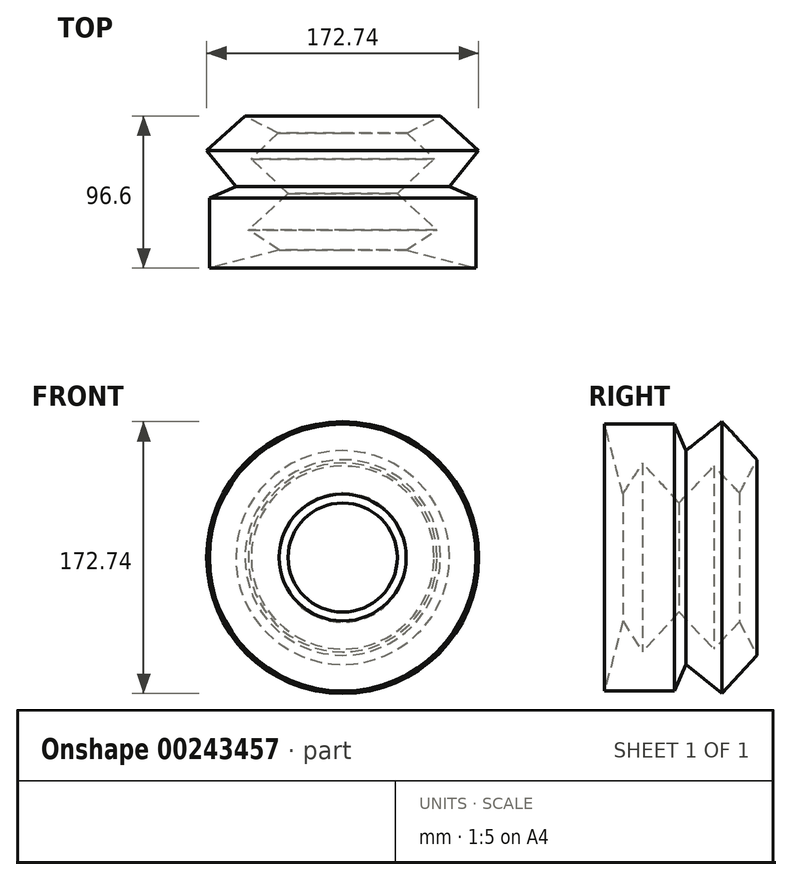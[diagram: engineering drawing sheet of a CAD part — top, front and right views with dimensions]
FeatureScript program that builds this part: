
annotation { "Feature Type Name" : "Feature", "Feature Type Description" : "" }
export const myFeature = defineFeature(function(context is Context, id is Id, definition is map)
    precondition{}
    {
        {
            var Q0;
            Q0=qCreatedBy(makeId("Top.planeOp"),FACE);
            var sketch = newSketch(context, id + "F0", { "sketchPlane" : qUnion([Q0])});
            skLineSegment(sketch, "E0", {"start": v(-10.73, 38.4) * mm, "end": v(6.44, 22.05) * mm});
            skLineSegment(sketch, "E1", {"start": v(6.44, 22.05) * mm, "end": v(-17, 0) * mm});
            skLineSegment(sketch, "E2", {"start": v(-17, 0) * mm, "end": v(8.26, -23.2) * mm});
            skLineSegment(sketch, "E3", {"start": v(8.26, -23.2) * mm, "end": v(-11.4, -35.75) * mm});
            skLineSegment(sketch, "E4", {"start": v(-11.4, -35.75) * mm, "end": v(33.03, -47.31) * mm});
            skLineSegment(sketch, "E5", {"start": v(33.03, -47.31) * mm, "end": v(33.03, -2.89) * mm});
            skLineSegment(sketch, "E6", {"start": v(33.03, -2.89) * mm, "end": v(16.18, 4.38) * mm});
            skLineSegment(sketch, "E7", {"start": v(16.18, 4.38) * mm, "end": v(34.68, 27.33) * mm});
            skLineSegment(sketch, "E8", {"start": v(34.68, 27.33) * mm, "end": v(10.4, 49.3) * mm});
            skLineSegment(sketch, "E9", {"start": v(10.4, 49.3) * mm, "end": v(-10.73, 38.4) * mm});
            skLineSegment(sketch, "E10", {"start": v(-51.69, 46) * mm, "end": v(-51.69, -40.05) * mm});
            skSolve(sketch);
        }
        {
            var Q0;
            Q0=makeQuery(id+"F0.imprint","IMPRINT",FACE,{"disambiguationData":[TD([[makeQuery(id+"F0.imprint","IMPRINT",EDGE,{"derivedFrom":sQuery(id+"F0.wireOp",EDGE,"E0")}),1.0]])]});
            var Q1;
            Q1=sQuery(id+"F0.wireOp",EDGE,"E10");
            revolve(context, id + "F1", {"entities" : qUnion([Q0]), "axis" : qUnion([Q1]), "revolveType" : RevolveType.FULL});
        }
    });
